# Revit family: Taylor_Entrance_8_Foot_High_Def_2_Panel
name_source: partatom
category: Doors
units: mm (PartAtom-declared; Revit-internal decimal feet)

## family parameters
Always vertical = Yes
Classification Number = 23.30.10.00
Cut with Voids When Loaded = No
Host = Wall
Room Calculation Point = No
Shared = No

## types (1)
- 36" x 96"
    Analytic Construction = <None>
    Description = 8'-0" high def 2 panel embossment for steel edge doors
    Door Finish = Door Finish - Grey Paintable Primer
    Door Frame Finish = Material - Door - Frame
    Function = Interior
    Height = 8' - 0"
    Manufacturer = Taylor Entrance Systems
    Manufacturer Fax = 800-252-5468
    Manufacturer Website = http://www.taylordoor.com
    Model = 8'-0" High Def 2 Panel
    Rough Height = 8' - 2"
    Rough Width = 3' - 4"
    Sales Information = http://www.taylordoor.com
    Specification = https://charrette.arcat.com
    Thickness = 0' - 1 3/4"
    Wall Closure = By host
    Width = 3' - 0"

## geometry (parser evidence)
native form markers: Sweep x5
no freeform markers — native parametric forms only
